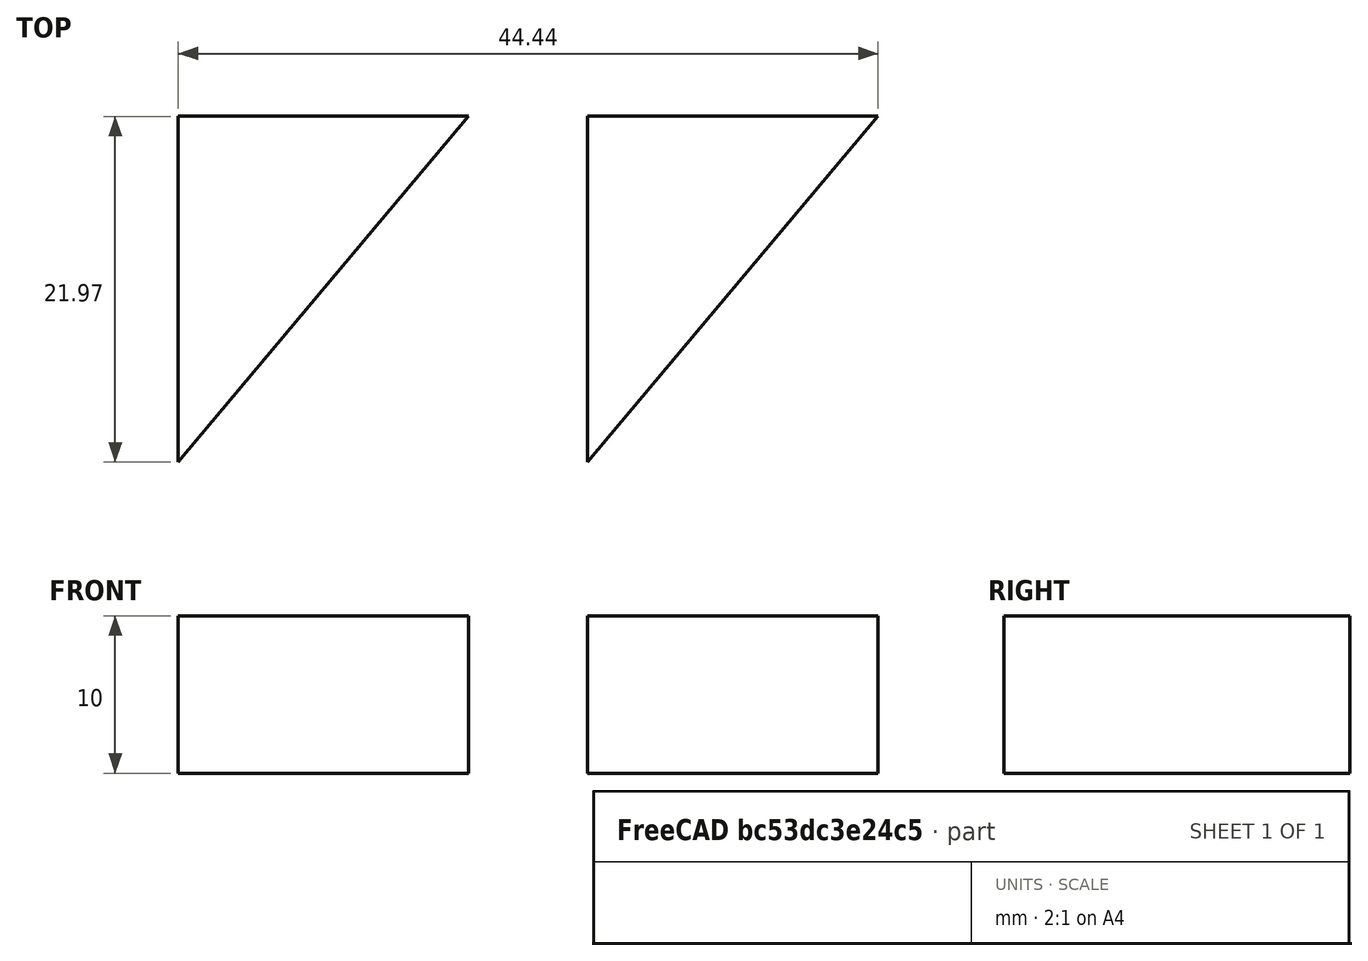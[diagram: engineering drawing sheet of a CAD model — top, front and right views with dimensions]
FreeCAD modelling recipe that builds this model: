
FCSTD DOCUMENT  (FreeCAD 1.0R39109 (Git))
Label: SupportAngleTesting
License: All rights reserved
LicenseURL: https://en.wikipedia.org/wiki/All_rights_reserved
objects: Part::Extrusion×2, Sketcher::SketchObject×1
note: 4 computed .brp shape members not serialized (recipe doc carries the construction recipe); baked Part::Feature solids carry a one-line shape summary decoded from their .brp

FEATURE [Sketcher::SketchObject] Sketch
  ArcFitTolerance = 1e-06
  FullyConstrained = false
  MakeInternals = false
  sketch-geometry (3):
    g0: LineSegment StartX=18.4367 StartY=21.972 StartZ=0 EndX=0 EndY=21.972 EndZ=0
    g1: LineSegment StartX=18.4367 StartY=21.972 StartZ=0 EndX=0 EndY=0 EndZ=0
    g2: LineSegment StartX=0 StartY=21.972 StartZ=0 EndX=0 EndY=0 EndZ=0
  constraints (7):
    c: PointOnObject(g0,g-2)
    c: Horizontal(g0)
    c: Coincident(g1,g0)
    c: Coincident(g1,g-1)
    c: Coincident(g2,g0)
    c: Coincident(g2,g1)
    c: Angle(g0,g1,g0) = 0.872665
FEATURE [Part::Extrusion] Extrude  label="FourtyFive"
  Base = -> Sketch
  Dir = (0,0,1)
  DirMode = 2
  FaceMakerClass = Part::FaceMakerBullseye
  FaceMakerMode = 3
  LengthFwd = 10
  LengthRev = 0
  Solid = true
  Symmetric = false
FEATURE [Part::Extrusion] Extrude001  label="Fifty"
  Base = -> Sketch
  Dir = (0,0,1)
  DirMode = 2
  FaceMakerClass = Part::FaceMakerBullseye
  FaceMakerMode = 3
  LengthFwd = 10
  LengthRev = 0
  Placement = pos=(-26,0,0) rot=(0,0,1;0rad)
  Solid = true
  Symmetric = false
